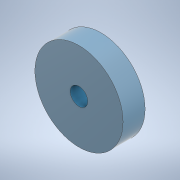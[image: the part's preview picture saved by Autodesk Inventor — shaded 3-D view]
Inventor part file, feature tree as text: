
AUTODESK INVENTOR PART (.ipt)
format: ipt  version: 2022 (Build 260153000, 153)  size: 117,248 bytes
history: native  units: mm
features: extrude x2, sketch x2
ambient origin geometry x8: Origin, YZ Plane, XZ Plane, XY Plane, X Axis, Y Axis, Z Axis, Center Point
bodies: Solid1 (feature_tree)
feature tree (4):
  extrude  "CounterWeight"  Depth=50.0mm TaperAngle=0.0deg
  extrude  "Extrusion2"  [1 undecoded]
  sketch  "Sketch1"  dims[d0=50.0mm d1=0.0mm d2=50.0mm d3=0.0mm]
  sketch  "Sketch2"
note: 1 required parameter value undecoded (feature->parameter linkage not recoverable at this tier; creation-order binding heuristic only, values carry confidence <= 0.55)
